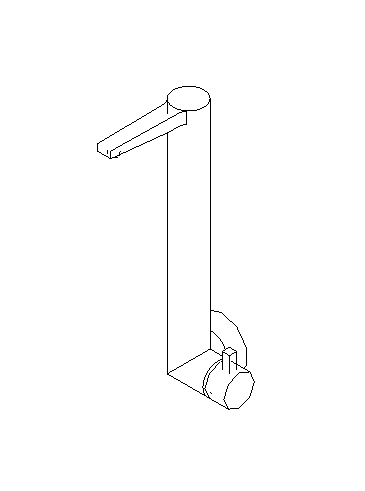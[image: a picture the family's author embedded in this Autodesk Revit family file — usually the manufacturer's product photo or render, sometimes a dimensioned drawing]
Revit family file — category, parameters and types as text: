
# Revit family: Deca_Filtro Single Parede Filtros Cozinha_1161.CFFFFF
name_source: partatom
category: Plumbing Fixtures
revit_build: Autodesk Revit Architecture 2012 (Build: 20120126_0600(x64)
units: mm (PartAtom-declared; Revit-internal decimal feet)

## types (1)
- 1161.C_Cromado CR10
    Aprovado por = Contino/quattroD
    Assembly Code = D2020
    Atendimento ao Cliente = 0800-0117073
    CWFU = 0
    Consumo = Varia com a pressão
    Criado por = Contino/quattroD
    Código = 1161.C
    Default Elevation = 0 mm  [stored 0 ft]
    Description = Filtro
    Diâmetro Água Fria = 15 mm  [stored 0.0492126 ft]
    Filtro = Deca CR10 Cromado Metal
    Flow Pressure = 0.00 psi
    HWFU = 0
    Informações Complementares = Mecanismo: 1/4 de volta
    Linha = Filtros Cozinha
    Louça/Metais = Metal
    Manufacturer = Deca
    Material = Deca_Latão Cromado e Plástico de Engenharia
    Model = 1161.C
    Norma = ABNT NBR 15267: 2005
    Peso Liquido (Kg) = 1.3
    Pressão = 2 A 40 mca
    Produto = Filtro Single Parede
    Raio Água Fria = 8 mm  [stored 0.0262467 ft]
    Segmento = Médio
    URL = www.deca.com.br/produtos
    Variações de COR = Cromado (1161.C).

note: [stored X ft] marks values corroborated as IEEE doubles in the binary element streams (Revit-internal decimal feet)

## geometry (parser evidence)
native form markers: Blend x2, Sweep x2
no freeform markers — native parametric forms only
